# Revit family: VIVREAU - Extra C-Tap - still-sparkling
name_source: partatom
category: Specialty Equipment
units: mm (PartAtom-declared; Revit-internal decimal feet)

## family parameters
Always vertical = Yes
Cut with Voids When Loaded = No
OmniClass Number = 23.40.40.00
OmniClass Title = Food Service Equipment and Furnishings
Part Type = Normal
Room Calculation Point = No
Round Connector Dimension = Use Diameter
Shared = No
Work Plane-Based = No

## types (1)
- VIV E 85 C-32-C2-TG
    Base Cabinet = BRITA_Base Cabinet_ENG : Base Cabinet 60 cm
    CLARITY Taste 100 = BRITA_CLARITY Taste 100_ENG : CLARITY Protect 100
    CO2 10 kg Bottle = BRITA_CO2 10kg Bottle_ENG : CO2 10 kg Bottle
    Conn Conduit = Yes
    Default Elevation = 0 mm
    Depth Actual = 600 mm
    Description = Extra C-Shape still & sparkling, Filter for cold water flow
    Equipment Designation = VIV E 85 C-32-C2-TG
    Extra C-Shape C2 = BRITA_Extra C-Shape C2_ENG : Extra C-Shape C2
    Foodservice Equipment Identifier = Yes
    Height Actual = 1139 mm
    Length Actual = 600 mm
    Manufacturer = BRITA GmbH
    Model = VIV E 85 C-32-C2-TG
    Tap 32 & Drip Tray = BRITA_Tap 32 and Drip Tray_ENG : Tap 32 & Drip Tray
    URL = www.brita.net
    URL Cutsheet = www.brita.net
    URL Manufacturer = www.brita.net
    URL Recommended Spares List = www.brita.net
    Weight = 0.00 kg

## geometry (parser evidence)
native form markers: Sweep x5
no freeform markers — native parametric forms only
